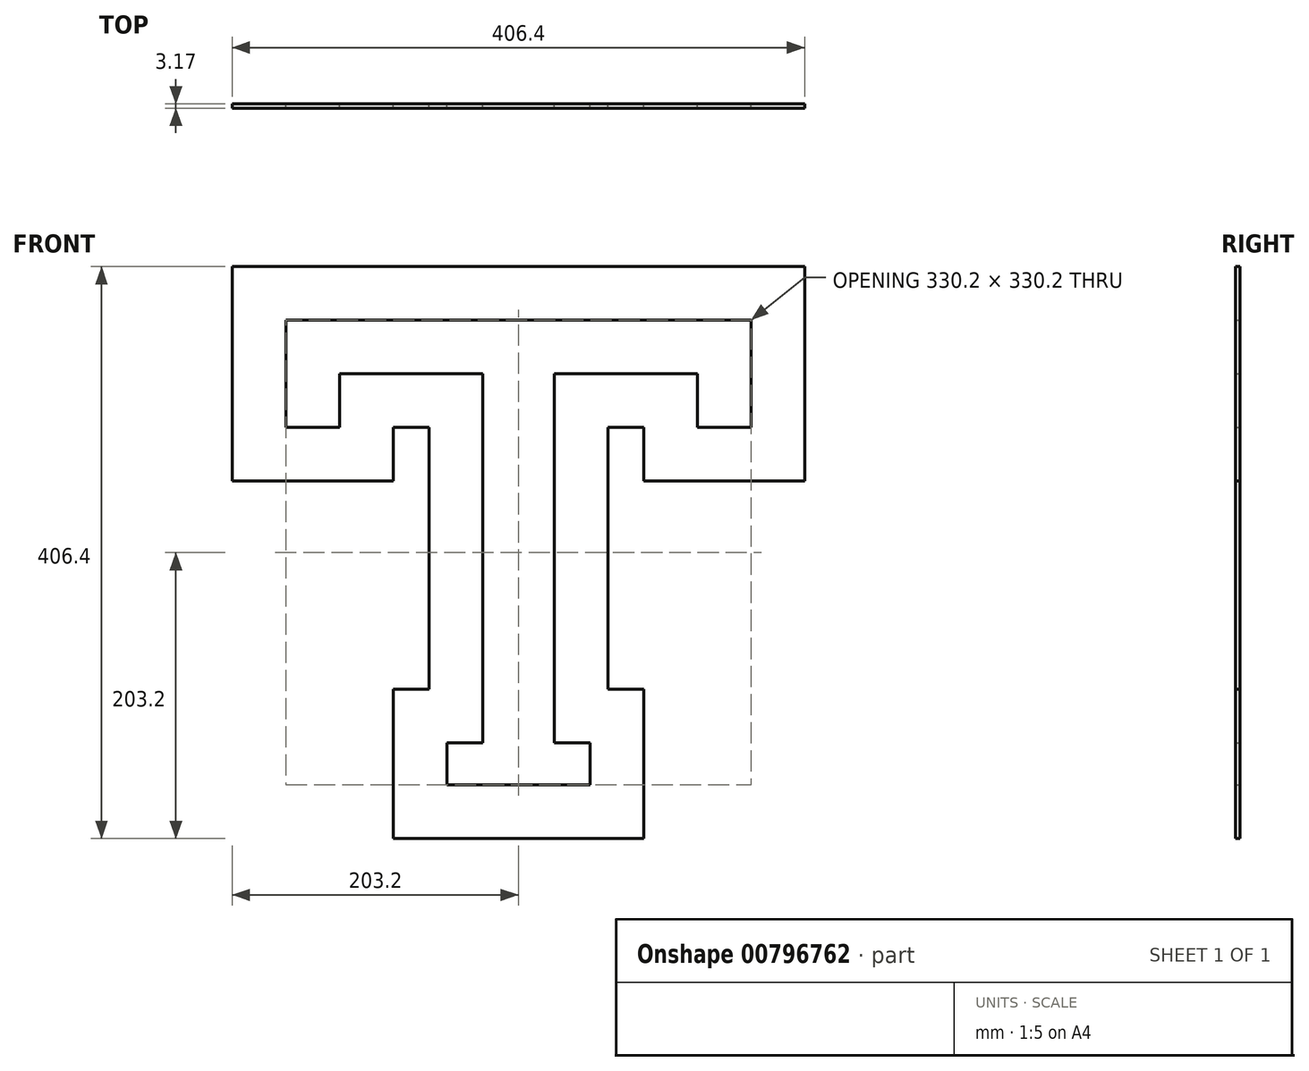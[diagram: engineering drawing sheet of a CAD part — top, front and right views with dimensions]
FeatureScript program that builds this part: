
annotation { "Feature Type Name" : "Feature", "Feature Type Description" : "" }
export const myFeature = defineFeature(function(context is Context, id is Id, definition is map)
    precondition{}
    {
        {
            var Q0;
            Q0=qCreatedBy(makeId("Front.planeOp"),FACE);
            var sketch = newSketch(context, id + "F0", { "sketchPlane" : qUnion([Q0])});
            skLineSegment(sketch, "E0.bottom", {"start": v(-25.4, 330.2) * mm, "end": v(0, 330.2) * mm});
            skLineSegment(sketch, "E0.top", {"start": v(-25.4, 0) * mm, "end": v(0, 0) * mm});
            skLineSegment(sketch, "E0.left", {"start": v(-25.4, 292.1) * mm, "end": v(-25.4, 30.02) * mm});
            skLineSegment(sketch, "E0.right", {"start": v(0, 330.2) * mm, "end": v(0, 0) * mm, "construction": true});
            skLineSegment(sketch, "E1.bottom", {"start": v(0, 330.2) * mm, "end": v(-165.1, 330.2) * mm});
            skLineSegment(sketch, "E1.top", {"start": v(-25.4, 292.1) * mm, "end": v(-127, 292.1) * mm});
            skLineSegment(sketch, "E1.left", {"start": v(0, 330.2) * mm, "end": v(0, 292.1) * mm});
            skLineSegment(sketch, "E1.right", {"start": v(-165.1, 330.2) * mm, "end": v(-165.1, 292.1) * mm});
            skLineSegment(sketch, "E2.bottom", {"start": v(-165.1, 330.2) * mm, "end": v(-127, 330.2) * mm});
            skLineSegment(sketch, "E2.top", {"start": v(-165.1, 254) * mm, "end": v(-127, 254) * mm});
            skLineSegment(sketch, "E2.left", {"start": v(-165.1, 330.2) * mm, "end": v(-165.1, 254) * mm});
            skLineSegment(sketch, "E2.right", {"start": v(-127, 292.1) * mm, "end": v(-127, 254) * mm});
            skLineSegment(sketch, "E3.bottom", {"start": v(0, 0) * mm, "end": v(-50.8, 0) * mm});
            skLineSegment(sketch, "E3.top", {"start": v(-25.4, 30.02) * mm, "end": v(-50.8, 30.02) * mm});
            skLineSegment(sketch, "E3.left", {"start": v(0, 0) * mm, "end": v(0, 30.02) * mm});
            skLineSegment(sketch, "E3.right", {"start": v(-50.8, 0) * mm, "end": v(-50.8, 30.02) * mm});
            skLineSegment(sketch, "E4.MirrorCS", {"start": v(0, 330.2) * mm, "end": v(165.1, 330.2) * mm});
            skLineSegment(sketch, "E5.MirrorCS", {"start": v(165.1, 330.2) * mm, "end": v(165.1, 254) * mm});
            skLineSegment(sketch, "E6.MirrorCS", {"start": v(165.1, 254) * mm, "end": v(127, 254) * mm});
            skLineSegment(sketch, "E7.MirrorCS", {"start": v(127, 292.1) * mm, "end": v(127, 254) * mm});
            skLineSegment(sketch, "E8.MirrorCS", {"start": v(25.4, 292.1) * mm, "end": v(127, 292.1) * mm});
            skLineSegment(sketch, "E9.MirrorCS", {"start": v(25.4, 292.1) * mm, "end": v(25.4, 30.02) * mm});
            skLineSegment(sketch, "E10.MirrorCS", {"start": v(25.4, 30.02) * mm, "end": v(50.8, 30.02) * mm});
            skLineSegment(sketch, "E11.MirrorCS", {"start": v(50.8, 0) * mm, "end": v(50.8, 30.02) * mm});
            skLineSegment(sketch, "E12.MirrorCS", {"start": v(0, 0) * mm, "end": v(50.8, 0) * mm});
            skLineSegment(sketch, "E13.0", {"start": v(-63.5, 254) * mm, "end": v(-88.9, 254) * mm});
            skLineSegment(sketch, "E13.1", {"start": v(-88.9, 254) * mm, "end": v(-88.9, 215.9) * mm});
            skLineSegment(sketch, "E13.2", {"start": v(-203.2, 215.9) * mm, "end": v(-88.9, 215.9) * mm});
            skLineSegment(sketch, "E13.3", {"start": v(-203.2, 368.3) * mm, "end": v(-203.2, 215.9) * mm});
            skLineSegment(sketch, "E13.4", {"start": v(0, 368.3) * mm, "end": v(-203.2, 368.3) * mm});
            skLineSegment(sketch, "E13.5", {"start": v(-63.5, 254) * mm, "end": v(-63.5, 68.12) * mm});
            skLineSegment(sketch, "E13.6", {"start": v(0, 368.3) * mm, "end": v(203.2, 368.3) * mm});
            skLineSegment(sketch, "E13.7", {"start": v(203.2, 368.3) * mm, "end": v(203.2, 215.9) * mm});
            skLineSegment(sketch, "E13.8", {"start": v(0, -38.1) * mm, "end": v(88.9, -38.1) * mm});
            skLineSegment(sketch, "E13.9", {"start": v(0, -38.1) * mm, "end": v(-88.9, -38.1) * mm});
            skLineSegment(sketch, "E13.10", {"start": v(-88.9, -38.1) * mm, "end": v(-88.9, 68.12) * mm});
            skLineSegment(sketch, "E13.11", {"start": v(-63.5, 68.12) * mm, "end": v(-88.9, 68.12) * mm});
            skLineSegment(sketch, "E13.12", {"start": v(88.9, -38.1) * mm, "end": v(88.9, 68.12) * mm});
            skLineSegment(sketch, "E13.13", {"start": v(63.5, 68.12) * mm, "end": v(88.9, 68.12) * mm});
            skLineSegment(sketch, "E13.14", {"start": v(63.5, 254) * mm, "end": v(63.5, 68.12) * mm});
            skLineSegment(sketch, "E13.15", {"start": v(63.5, 254) * mm, "end": v(88.9, 254) * mm});
            skLineSegment(sketch, "E13.16", {"start": v(88.9, 254) * mm, "end": v(88.9, 215.9) * mm});
            skLineSegment(sketch, "E13.17", {"start": v(203.2, 215.9) * mm, "end": v(88.9, 215.9) * mm});
            skSolve(sketch);
        }
        {
            var Q0;
            {var subQ1=sQuery(id+"F0.wireOp",EDGE,"E0.bottom");Q0=makeQuery(id+"F0.imprint","IMPRINT",FACE,{"disambiguationData":[TD([[makeQuery(id+"F0.imprint","IMPRINT",EDGE,{"derivedFrom":subQ1}),1.0]])]});}
            extrude(context, id + "F1", {"entities" : qUnion([Q0]), "depth" : 3.17 * mm, "offsetDistance" : 25.4 * mm});
        }
    });
